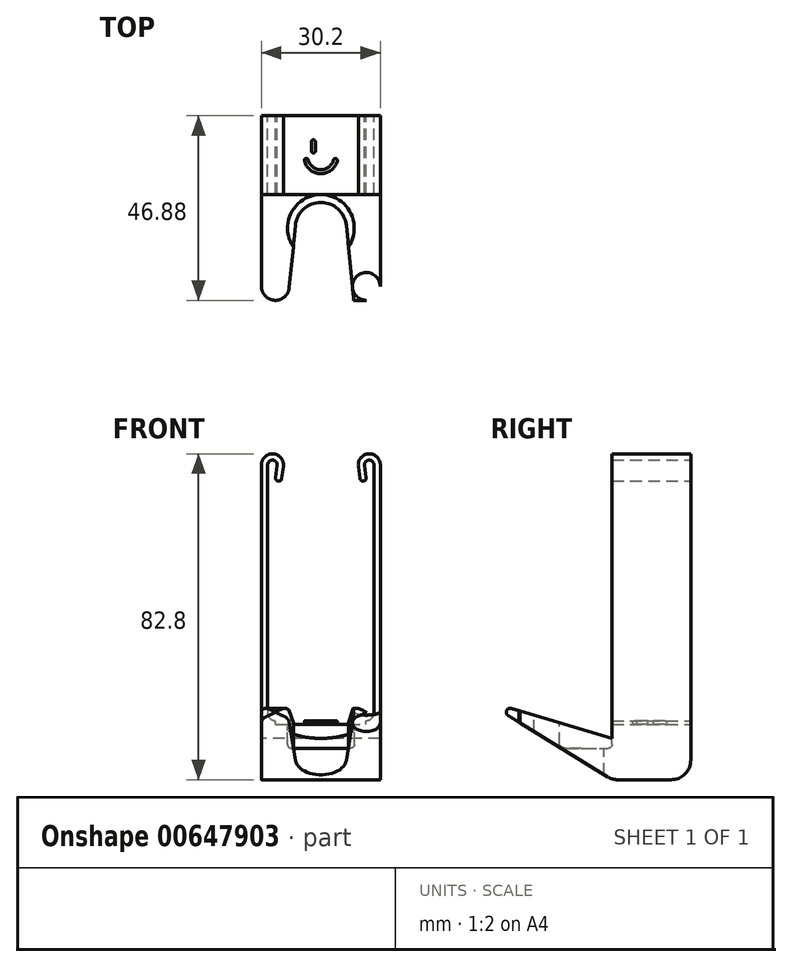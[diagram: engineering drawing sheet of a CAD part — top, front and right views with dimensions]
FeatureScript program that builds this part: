
annotation { "Feature Type Name" : "Feature", "Feature Type Description" : "" }
export const myFeature = defineFeature(function(context is Context, id is Id, definition is map)
    precondition{}
    {
        {
            var Q0;
            Q0=qCreatedBy(makeId("Front.planeOp"),FACE);
            var sketch = newSketch(context, id + "F0", { "sketchPlane" : qUnion([Q0])});
            skLineSegment(sketch, "E0.bottom", {"start": v(-11.5, -36.45) * mm, "end": v(0, -36.45) * mm});
            skLineSegment(sketch, "E0.top", {"start": v(-15.1, -51.45) * mm, "end": v(0, -51.45) * mm});
            skLineSegment(sketch, "E0.left", {"start": v(-15.1, -36.45) * mm, "end": v(-15.1, -51.45) * mm});
            skLineSegment(sketch, "E0.right", {"start": v(0, -36.45) * mm, "end": v(0, -51.45) * mm});
            skArc(sketch, "E1", {"start": v(-9.52, 28.18) * mm, "mid": v(-12.12, 31.34) * mm, "end": v(-15.1, 28.55) * mm});
            skLineSegment(sketch, "E2", {"start": v(-15.1, 28.55) * mm, "end": v(-15.1, -36.45) * mm});
            skLineSegment(sketch, "E3", {"start": v(-13.5, 28.55) * mm, "end": v(-13.5, -34.45) * mm});
            skPoint(sketch, "E4.visualSharp", {"position": v(-13.5, -36.45) * mm});
            skArc(sketch, "E4.filletArc", {"start": v(-13.5, -34.45) * mm, "mid": v(-12.91, -35.87) * mm, "end": v(-11.5, -36.45) * mm});
            skArc(sketch, "E5", {"start": v(-11.11, 28.4) * mm, "mid": v(-12.22, 29.75) * mm, "end": v(-13.5, 28.55) * mm});
            skLineSegment(sketch, "E6", {"start": v(-12.3, 28.55) * mm, "end": v(-9.52, 28.18) * mm, "construction": true});
            skLineSegment(sketch, "E7", {"start": v(-11.11, 28.4) * mm, "end": v(-11.52, 25.3) * mm});
            skLineSegment(sketch, "E8", {"start": v(-9.52, 28.18) * mm, "end": v(-9.93, 25.1) * mm});
            skArc(sketch, "E9", {"start": v(-11.52, 25.3) * mm, "mid": v(-10.83, 24.4) * mm, "end": v(-9.93, 25.1) * mm});
            skSolve(sketch);
        }
        {
            var Q0;
            Q0=makeQuery(id+"F0.imprint","IMPRINT",FACE,{"disambiguationData":[TD([[makeQuery(id+"F0.imprint","IMPRINT",EDGE,{"derivedFrom":sQuery(id+"F0.wireOp",EDGE,"E0.bottom")}),-1.0]])]});
            var Q1;
            {var subQ1=sQuery(id+"F0.wireOp",EDGE,"2DHoUzyD-ZS0R-mkVg-75mC-VmwePcq2ybin");Q1=makeQuery(id+"F0.imprint","IMPRINT",FACE,{"disambiguationData":[TD([[makeQuery(id+"F0.imprint","IMPRINT",EDGE,{"derivedFrom":subQ1}),-1.0]])]});}
            var Q2;
            {var subQ3=sQuery(id+"F0.wireOp",EDGE,"E5");Q2=makeQuery(id+"F0.imprint","IMPRINT",FACE,{"disambiguationData":[TD([[makeQuery(id+"F0.imprint","IMPRINT",EDGE,{"derivedFrom":subQ3}),-1.0]])]});}
            extrude(context, id + "F1", {"entities" : qUnion([Q0, Q1, Q2]), "depth" : 20 * mm, "offsetDistance" : 25 * mm});
        }
        {
            var Q0;
            Q0=makeQuery(id+"F1.opExtrude","SWEPT_BODY",BODY,{"disambiguationData":[OSD([sQuery(id+"F0.wireOp",EDGE,"2DHoUzyD-ZS0R-mkVg-75mC-VmwePcq2ybin"),sQuery(id+"F0.wireOp",EDGE,"E0.bottom"),sQuery(id+"F0.wireOp",EDGE,"E0.top"),sQuery(id+"F0.wireOp",EDGE,"E0.left"),sQuery(id+"F0.wireOp",EDGE,"E0.right"),sQuery(id+"F0.wireOp",EDGE,"E1"),sQuery(id+"F0.wireOp",EDGE,"E2"),sQuery(id+"F0.wireOp",EDGE,"E3"),sQuery(id+"F0.wireOp",EDGE,"BcAyQxaD-hsAo-XjjC-ZKuc-NvUQVHeIa6M2"),sQuery(id+"F0.wireOp",EDGE,"7319f21d-551e-4965-8946-005827835c29.filletArc"),sQuery(id+"F0.wireOp",EDGE,"E4.filletArc")])]});
            var Q1;
            Q1=makeQuery(id+"F1.opExtrude","SWEPT_FACE",FACE,{"disambiguationData":[OSD([sQuery(id+"F0.wireOp",EDGE,"E0.right")])]});
            mirror(context, id + "F2", {"operationType" : NewBodyOperationType.ADD, "entities" : qUnion([Q0]), "mirrorPlane" : qUnion([Q1])});
        }
        {
            var Q0;
            Q0=makeQuery(id+"F1.opExtrude","SWEPT_FACE",FACE,{"disambiguationData":[OSD([sQuery(id+"F0.wireOp",EDGE,"E0.left"),sQuery(id+"F0.wireOp",EDGE,"E2")])]});
            var sketch = newSketch(context, id + "F3", { "sketchPlane" : qUnion([Q0])});
            skLineSegment(sketch, "E10", {"start": v(20, -51.45) * mm, "end": v(46.4, -35.15) * mm});
            skLineSegment(sketch, "E11", {"start": v(45.6, -33.34) * mm, "end": v(20, -40.94) * mm});
            skPoint(sketch, "E12.visualSharp", {"position": v(52.8, -31.2) * mm});
            skArc(sketch, "E12.filletArc", {"start": v(46.4, -35.15) * mm, "mid": v(46.8, -33.89) * mm, "end": v(45.6, -33.34) * mm});
            skSolve(sketch);
        }
        {
            var Q0;
            {var subQ0=sQuery(id+"F3.wireOp",EDGE,"E10");Q0=makeQuery(id+"F3.imprint","IMPRINT",FACE,{"disambiguationData":[TD([[makeQuery(id+"F3.imprint","IMPRINT",EDGE,{"derivedFrom":subQ0}),1.0]])]});}
            var Q1;
            Q1=makeQuery(id+"F2.opPattern","COPY",FACE,{"derivedFrom":makeQuery(id+"F1.opExtrude","SWEPT_FACE",FACE,{"disambiguationData":[OSD([sQuery(id+"F0.wireOp",EDGE,"E0.left"),sQuery(id+"F0.wireOp",EDGE,"E2")])]}),"instanceName":"1"});
            extrude(context, id + "F4", {"entities" : qUnion([Q0]), "operationType" : NewBodyOperationType.ADD, "endBound" : BoundingType.UP_TO_SURFACE, "oppositeDirection" : true, "depth" : 25 * mm, "endBoundEntityFace" : qUnion([Q1]), "offsetDistance" : 25 * mm});
        }
        {
            var Q0;
            {var subQ0=sQuery(id+"F0.wireOp",EDGE,"E0.top");var subQ1=makeQuery(id+"F1.opExtrude","CAP_EDGE",EDGE,{"disambiguationData":[OSD([subQ0])],"isStart":false});Q0=makeQuery(id+"F4.boolean.opBoolean","MERGE",EDGE,{"derivedFrom":[makeQuery(id+"F2.boolean.opBoolean","MERGE",EDGE,{"derivedFrom":[subQ1,makeQuery(id+"F2.opPattern","COPY",EDGE,{"derivedFrom":subQ1,"instanceName":"1"})]}),makeQuery(id+"F4.opExtrude","SWEPT_EDGE",EDGE,{"disambiguationData":[OSD([subQ0,sQuery(id+"F0.wireOp",EDGE,"E0.left"),sQuery(id+"F0.wireOp",EDGE,"E2"),sQuery(id+"F3.wireOp",EDGE,"E10")])]})]});}
            var Q1;
            {var subQ0=makeQuery(id+"F1.opExtrude","CAP_EDGE",EDGE,{"disambiguationData":[OSD([sQuery(id+"F0.wireOp",EDGE,"E0.top")])],"isStart":true});Q1=makeQuery(id+"F2.boolean.opBoolean","MERGE",EDGE,{"derivedFrom":[subQ0,makeQuery(id+"F2.opPattern","COPY",EDGE,{"derivedFrom":subQ0,"instanceName":"1"})]});}
            fillet(context, id + "F5", {"entities" : qUnion([Q0, Q1]), "radius" : 5 * mm, "tangentPropagation" : true, "allowEdgeOverflow" : false});
        }
        {
            var Q0;
            {var subQ0=makeQuery(id+"F1.opExtrude","SWEPT_FACE",FACE,{"disambiguationData":[OSD([sQuery(id+"F0.wireOp",EDGE,"E0.bottom")])]});Q0=makeQuery(id+"F2.boolean.opBoolean","MERGE",FACE,{"derivedFrom":[subQ0,makeQuery(id+"F2.opPattern","COPY",FACE,{"derivedFrom":subQ0,"instanceName":"1"})]});}
            var sketch = newSketch(context, id + "F6", { "sketchPlane" : qUnion([Q0])});
            skArc(sketch, "E13", {"start": v(6.47, -27.86) * mm, "mid": v(0, -22) * mm, "end": v(-6.47, -27.86) * mm});
            skLineSegment(sketch, "E14", {"start": v(-6.47, -27.86) * mm, "end": v(-8.35, -46.88) * mm});
            skLineSegment(sketch, "E15", {"start": v(0, -11.3) * mm, "end": v(0, -35) * mm, "construction": true});
            skLineSegment(sketch, "E16.MirrorCS", {"start": v(6.47, -27.86) * mm, "end": v(8.35, -46.88) * mm});
            skLineSegment(sketch, "E17", {"start": v(-8.35, -46.88) * mm, "end": v(8.35, -46.88) * mm});
            skLineSegment(sketch, "E18.0", {"start": v(15.1, -20) * mm, "end": v(-15.1, -20) * mm});
            skArc(sketch, "E19", {"start": v(0, -20) * mm, "mid": v(-7.52, -24.54) * mm, "end": v(-7, -33.3) * mm});
            skArc(sketch, "E20.trimOffspring", {"start": v(7, -33.3) * mm, "mid": v(7.52, -24.54) * mm, "end": v(0, -20) * mm});
            skLineSegment(sketch, "E21.0.0", {"start": v(15.1, -45.6) * mm, "end": v(15.1, -46.88) * mm});
            skLineSegment(sketch, "E21.0.2", {"start": v(-15.1, -45.6) * mm, "end": v(-15.1, -46.88) * mm});
            skLineSegment(sketch, "E22", {"start": v(-15.1, -46.88) * mm, "end": v(-8.35, -46.88) * mm});
            skLineSegment(sketch, "E23.trimOffspring", {"start": v(8.35, -46.88) * mm, "end": v(15.1, -46.88) * mm});
            skCircle(sketch, "E24", {"center": v(-11.56, -43.34) * mm, "radius": 3.54 * mm});
            skCircle(sketch, "E25.MirrorC", {"center": v(11.56, -43.34) * mm, "radius": 3.54 * mm});
            skLineSegment(sketch, "E26.0", {"start": v(-15.1, -45.6) * mm, "end": v(-15.1, -20) * mm});
            skLineSegment(sketch, "E26.1", {"start": v(15.1, -20) * mm, "end": v(15.1, -45.6) * mm});
            skSolve(sketch);
        }
        {
            var Q0;
            Q0=makeQuery(id+"F6.imprint","IMPRINT",FACE,{"disambiguationData":[TD([[makeQuery(id+"F6.imprint","IMPRINT",EDGE,{"derivedFrom":sQuery(id+"F6.wireOp",EDGE,"E13")}),1.0]])]});
            var Q1;
            {var subQ0=sQuery(id+"F6.wireOp",EDGE,"E22");var subQ3=sQuery(id+"F6.wireOp",EDGE,"E24");var subQ5=makeQuery(id+"F6.imprint","INTERSECT",VERTEX,{"derivedFrom":[subQ0,subQ3]});Q1=makeQuery(id+"F6.imprint","IMPRINT",FACE,{"disambiguationData":[TD([[makeQuery(id+"F6.imprint","IMPRINT",EDGE,{"disambiguationData":[TD([[subQ5,-1.0]])],"derivedFrom":subQ3}),-1.0]])]});}
            var Q2;
            {var subQ0=sQuery(id+"F6.wireOp",EDGE,"E21.0.2");Q2=makeQuery(id+"F6.imprint","IMPRINT",FACE,{"disambiguationData":[TD([[makeQuery(id+"F6.imprint","IMPRINT",EDGE,{"derivedFrom":subQ0}),1.0]])]});}
            var Q3;
            {var subQ0=sQuery(id+"F6.wireOp",EDGE,"E21.0.0");Q3=makeQuery(id+"F6.imprint","IMPRINT",FACE,{"disambiguationData":[TD([[makeQuery(id+"F6.imprint","IMPRINT",EDGE,{"derivedFrom":subQ0}),-1.0]])]});}
            var Q4;
            {var subQ0=sQuery(id+"F6.wireOp",EDGE,"E23.trimOffspring");var subQ3=sQuery(id+"F6.wireOp",EDGE,"E25.MirrorC");var subQ5=makeQuery(id+"F6.imprint","INTERSECT",VERTEX,{"derivedFrom":[subQ0,subQ3]});Q4=makeQuery(id+"F6.imprint","IMPRINT",FACE,{"disambiguationData":[TD([[makeQuery(id+"F6.imprint","IMPRINT",EDGE,{"disambiguationData":[TD([[subQ5,-1.0]])],"derivedFrom":subQ3}),1.0]])]});}
            extrude(context, id + "F7", {"entities" : qUnion([Q0, Q1, Q2, Q3, Q4]), "operationType" : NewBodyOperationType.REMOVE, "endBound" : BoundingType.THROUGH_ALL, "oppositeDirection" : true, "depth" : 25 * mm, "offsetDistance" : 25 * mm, "hasSecondDirection" : true, "secondDirectionBound" : SecondDirectionBoundingType.THROUGH_ALL, "secondDirectionOppositeDirection" : false, "secondDirectionDepth" : 25 * mm});
        }
        {
            var Q0;
            {var subQ5=sQuery(id+"F6.wireOp",EDGE,"E19");Q0=makeQuery(id+"F6.imprint","IMPRINT",FACE,{"disambiguationData":[TD([[makeQuery(id+"F6.imprint","IMPRINT",EDGE,{"derivedFrom":subQ5}),1.0]])]});}
            var Q1;
            {var subQ5=sQuery(id+"F6.wireOp",EDGE,"E20.trimOffspring");Q1=makeQuery(id+"F6.imprint","IMPRINT",FACE,{"disambiguationData":[TD([[makeQuery(id+"F6.imprint","IMPRINT",EDGE,{"derivedFrom":subQ5}),1.0]])]});}
            extrude(context, id + "F8", {"entities" : qUnion([Q0, Q1]), "operationType" : NewBodyOperationType.REMOVE, "oppositeDirection" : true, "depth" : 7 * mm, "offsetDistance" : 25 * mm});
        }
        {
            var Q0;
            Q0=makeQuery(id+"F8.boolean.opBoolean","COPY",EDGE,{"derivedFrom":makeQuery(id+"F8.opExtrude","CAP_EDGE",EDGE,{"disambiguationData":[OSD([sQuery(id+"F6.wireOp",EDGE,"E19")])],"isStart":false})});
            var Q1;
            Q1=makeQuery(id+"F8.boolean.opBoolean","COPY",EDGE,{"derivedFrom":makeQuery(id+"F8.opExtrude","CAP_EDGE",EDGE,{"disambiguationData":[OSD([sQuery(id+"F6.wireOp",EDGE,"E20.trimOffspring")])],"isStart":false})});
            fillet(context, id + "F9", {"entities" : qUnion([Q0, Q1]), "radius" : 1 * mm, "tangentPropagation" : true, "allowEdgeOverflow" : false});
        }
        {
            var Q0;
            {var subQ0=makeQuery(id+"F1.opExtrude","SWEPT_FACE",FACE,{"disambiguationData":[OSD([sQuery(id+"F0.wireOp",EDGE,"E0.bottom")])]});Q0=makeQuery(id+"F2.boolean.opBoolean","MERGE",FACE,{"derivedFrom":[subQ0,makeQuery(id+"F2.opPattern","COPY",FACE,{"derivedFrom":subQ0,"instanceName":"1"})]});}
            var sketch = newSketch(context, id + "F10", { "sketchPlane" : qUnion([Q0])});
            skLineSegment(sketch, "E27", {"start": v(-1.89, -6.6) * mm, "end": v(-1.89, -8.95) * mm});
            skArc(sketch, "E28.0.startCap", {"start": v(-2.39, -6.6) * mm, "mid": v(-1.89, -6.1) * mm, "end": v(-1.39, -6.6) * mm});
            skArc(sketch, "E28.0.endCap", {"start": v(-1.39, -8.95) * mm, "mid": v(-1.89, -9.45) * mm, "end": v(-2.39, -8.95) * mm});
            skLineSegment(sketch, "E28.0.left", {"start": v(-1.39, -6.6) * mm, "end": v(-1.39, -8.95) * mm});
            skLineSegment(sketch, "E28.0.right", {"start": v(-2.39, -6.6) * mm, "end": v(-2.39, -8.95) * mm});
            skLineSegment(sketch, "E29.MirrorCS", {"start": v(2.39, -6.6) * mm, "end": v(2.39, -8.95) * mm});
            skLineSegment(sketch, "E30.MirrorCS", {"start": v(1.39, -6.6) * mm, "end": v(1.39, -8.95) * mm});
            skArc(sketch, "E31.MirrorCS", {"start": v(2.39, -6.6) * mm, "mid": v(1.89, -6.1) * mm, "end": v(1.39, -6.6) * mm});
            skLineSegment(sketch, "E32.MirrorCS", {"start": v(1.89, -6.6) * mm, "end": v(1.89, -8.95) * mm});
            skArc(sketch, "E33.MirrorCS", {"start": v(1.39, -8.95) * mm, "mid": v(1.89, -9.45) * mm, "end": v(2.39, -8.95) * mm});
            skArc(sketch, "E34", {"start": v(-3.7, -11.33) * mm, "mid": v(-2.34, -13.4) * mm, "end": v(0, -14.2) * mm});
            skArc(sketch, "E35.MirrorCS", {"start": v(3.7, -11.33) * mm, "mid": v(2.34, -13.4) * mm, "end": v(0, -14.2) * mm});
            skArc(sketch, "E36.0.startCap", {"start": v(-4.18, -11.45) * mm, "mid": v(-3.82, -10.84) * mm, "end": v(-3.2, -11.2) * mm});
            skArc(sketch, "E36.0.left", {"start": v(-3.2, -11.2) * mm, "mid": v(-2.03, -13) * mm, "end": v(0, -13.7) * mm});
            skArc(sketch, "E36.0.right", {"start": v(-4.18, -11.45) * mm, "mid": v(-2.65, -13.8) * mm, "end": v(0, -14.7) * mm});
            skArc(sketch, "E36.1.startCap", {"start": v(3.2, -11.2) * mm, "mid": v(3.82, -10.84) * mm, "end": v(4.18, -11.45) * mm});
            skArc(sketch, "E36.1.left", {"start": v(4.18, -11.45) * mm, "mid": v(2.65, -13.8) * mm, "end": v(0, -14.7) * mm});
            skArc(sketch, "E36.1.right", {"start": v(3.2, -11.2) * mm, "mid": v(2.03, -13) * mm, "end": v(0, -13.7) * mm});
            skSolve(sketch);
        }
        {
            var Q0;
            Q0=makeQuery(id+"F10.imprint","IMPRINT",FACE,{"disambiguationData":[TD([[makeQuery(id+"F10.imprint","IMPRINT",EDGE,{"derivedFrom":sQuery(id+"F10.wireOp",EDGE,"E28.0.startCap")}),-1.0]])]});
            var Q1;
            Q1=makeQuery(id+"F10.imprint","IMPRINT",FACE,{"disambiguationData":[TD([[makeQuery(id+"F10.imprint","IMPRINT",EDGE,{"derivedFrom":sQuery(id+"F10.wireOp",EDGE,"E29.MirrorCS")}),-1.0]])]});
            var Q2;
            Q2=makeQuery(id+"F10.imprint","IMPRINT",FACE,{"disambiguationData":[TD([[makeQuery(id+"F10.imprint","IMPRINT",EDGE,{"derivedFrom":sQuery(id+"F10.wireOp",EDGE,"E36.0.startCap")}),-1.0]])]});
            extrude(context, id + "F11", {"entities" : qUnion([Q0, Q1, Q2]), "operationType" : NewBodyOperationType.REMOVE, "oppositeDirection" : true, "depth" : 1 * mm, "offsetDistance" : 25 * mm});
        }
        {
            var Q0;
            Q0=makeQuery(id+"F11.boolean.opBoolean","COPY",EDGE,{"derivedFrom":makeQuery(id+"F11.opExtrude","CAP_EDGE",EDGE,{"disambiguationData":[OSD([sQuery(id+"F10.wireOp",EDGE,"E30.MirrorCS")])],"isStart":true})});
            var Q1;
            Q1=makeQuery(id+"F11.boolean.opBoolean","COPY",EDGE,{"derivedFrom":makeQuery(id+"F11.opExtrude","CAP_EDGE",EDGE,{"disambiguationData":[OSD([sQuery(id+"F10.wireOp",EDGE,"E28.0.right")])],"isStart":true})});
            var Q2;
            Q2=makeQuery(id+"F11.boolean.opBoolean","COPY",EDGE,{"derivedFrom":makeQuery(id+"F11.opExtrude","CAP_EDGE",EDGE,{"disambiguationData":[OSD([sQuery(id+"F10.wireOp",EDGE,"E36.0.left"),sQuery(id+"F10.wireOp",EDGE,"E36.1.right")])],"isStart":true})});
            fillet(context, id + "F12", {"entities" : qUnion([Q0, Q1, Q2]), "radius" : .3 * mm, "tangentPropagation" : true, "allowEdgeOverflow" : false});
        }
    });
